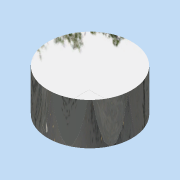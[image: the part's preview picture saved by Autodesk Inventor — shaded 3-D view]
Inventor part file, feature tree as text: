
AUTODESK INVENTOR PART (.ipt)
format: ipt  version: 2015 (Build 190159000, 159)  size: 82,944 bytes
history: native  units: in
note: dims shown in document units (in); Inventor stores cm internally (conversion verified against a paired STEP export)
features: extrude x1, sketch x1
ambient origin geometry x8: Origin, YZ Plane, XZ Plane, XY Plane, X Axis, Y Axis, Z Axis, Center Point
bodies: Solid1 (feature_tree)
feature tree (2):
  extrude  "Extrusion1"  Depth=0.125in TaperAngle=0.0deg
  sketch  "Sketch1"  dims[d0=0.25in d1=0.125in d2=0.0in]
